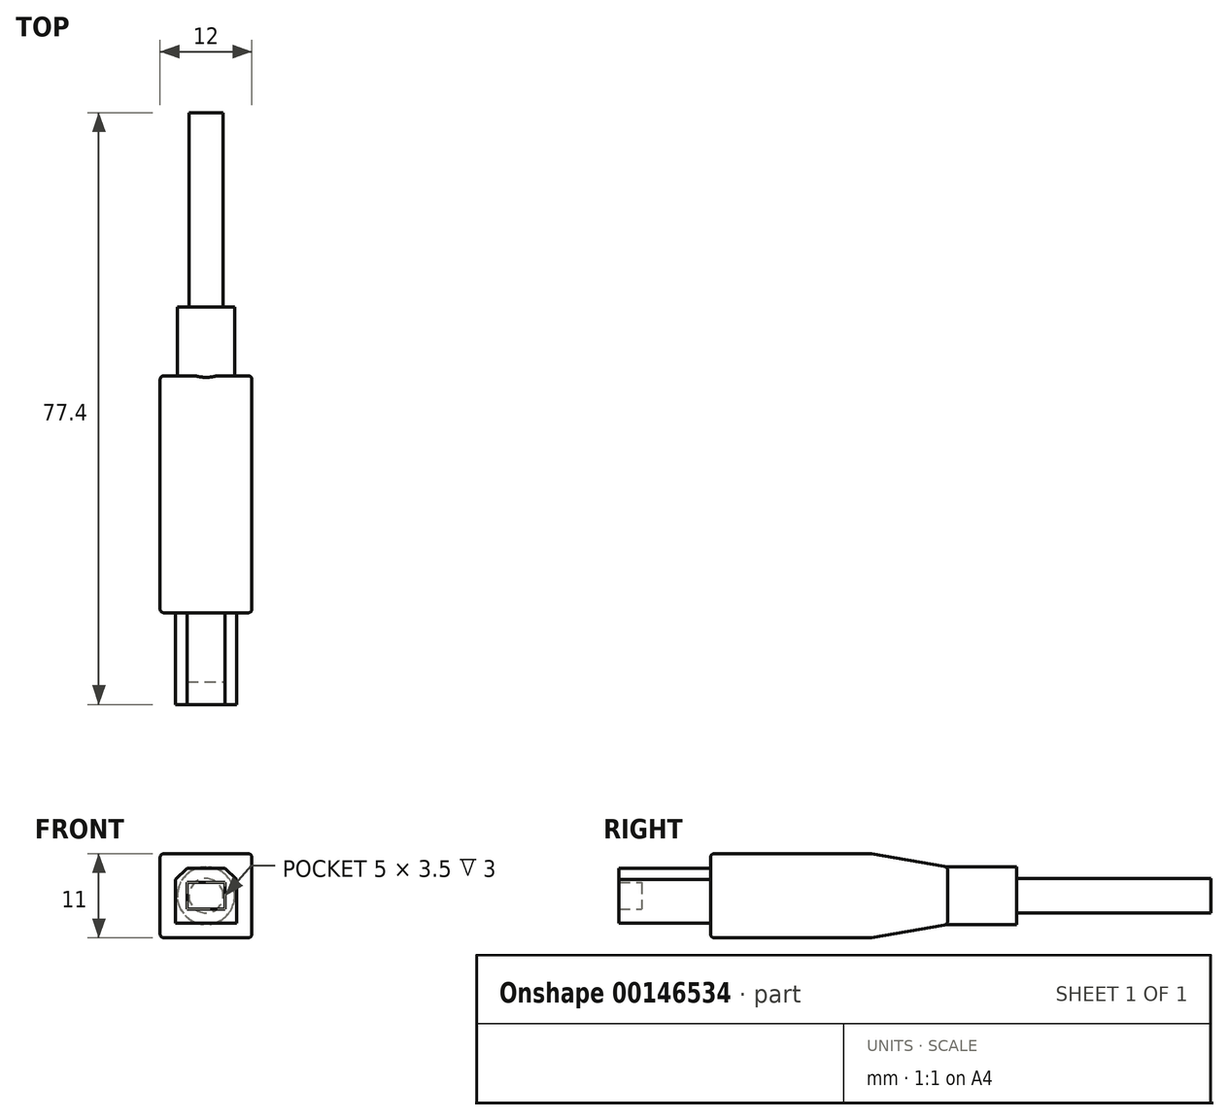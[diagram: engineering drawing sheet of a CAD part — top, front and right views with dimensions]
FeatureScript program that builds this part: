
annotation { "Feature Type Name" : "Feature", "Feature Type Description" : "" }
export const myFeature = defineFeature(function(context is Context, id is Id, definition is map)
    precondition{}
    {
        {
            var Q0;
            Q0=qCreatedBy(makeId("Front.planeOp"),FACE);
            var sketch = newSketch(context, id + "F0", { "sketchPlane" : qUnion([Q0])});
            skLineSegment(sketch, "E0.bottom", {"start": v(6, -5.5) * mm, "end": v(-6, -5.5) * mm});
            skLineSegment(sketch, "E0.top", {"start": v(6, 5.5) * mm, "end": v(-6, 5.5) * mm});
            skLineSegment(sketch, "E0.left", {"start": v(6, -5.5) * mm, "end": v(6, 5.5) * mm});
            skLineSegment(sketch, "E0.right", {"start": v(-6, -5.5) * mm, "end": v(-6, 5.5) * mm});
            skPoint(sketch, "E0.middle", {"position": v(0, 0) * mm});
            skLineSegment(sketch, "E1.bottom", {"start": v(-2.5, 1.75) * mm, "end": v(2.5, 1.75) * mm});
            skLineSegment(sketch, "E1.top", {"start": v(-2.5, -1.75) * mm, "end": v(2.5, -1.75) * mm});
            skLineSegment(sketch, "E1.left", {"start": v(-2.5, 1.75) * mm, "end": v(-2.5, -1.75) * mm});
            skLineSegment(sketch, "E1.right", {"start": v(2.5, 1.75) * mm, "end": v(2.5, -1.75) * mm});
            skLineSegment(sketch, "E2.bottom", {"start": v(-4, 3.6) * mm, "end": v(4, 3.6) * mm});
            skLineSegment(sketch, "E2.top", {"start": v(-4, -3.6) * mm, "end": v(4, -3.6) * mm});
            skLineSegment(sketch, "E2.left", {"start": v(-4, 3.6) * mm, "end": v(-4, -3.6) * mm});
            skLineSegment(sketch, "E2.right", {"start": v(4, 3.6) * mm, "end": v(4, -3.6) * mm});
            skPoint(sketch, "E3", {"position": v(0, 3.6) * mm});
            skPoint(sketch, "E4", {"position": v(-4, 0) * mm});
            skPoint(sketch, "E5", {"position": v(-2.5, 0) * mm});
            skPoint(sketch, "E6", {"position": v(0, 1.75) * mm});
            skSolve(sketch);
        }
        {
            var Q0;
            Q0=makeQuery(id+"F0.imprint","IMPRINT",FACE,{"disambiguationData":[TD([[makeQuery(id+"F0.imprint","IMPRINT",EDGE,{"derivedFrom":sQuery(id+"F0.wireOp",EDGE,"E1.bottom")}),1.0]])]});
            extrude(context, id + "F1", {"entities" : qUnion([Q0]), "depth" : 12 * mm});
        }
        {
            var Q0;
            Q0=makeQuery(id+"F0.imprint","IMPRINT",FACE,{"disambiguationData":[TD([[makeQuery(id+"F0.imprint","IMPRINT",EDGE,{"derivedFrom":sQuery(id+"F0.wireOp",EDGE,"E1.bottom")}),-1.0]])]});
            extrude(context, id + "F2", {"entities" : qUnion([Q0]), "operationType" : NewBodyOperationType.ADD, "depth" : 9 * mm});
        }
        {
            var Q0;
            Q0=makeQuery(id+"F1.opExtrude","SWEPT_EDGE",EDGE,{"disambiguationData":[OSD([sQuery(id+"F0.wireOp",EDGE,"E2.bottom"),sQuery(id+"F0.wireOp",EDGE,"E2.left")])]});
            var Q1;
            Q1=makeQuery(id+"F1.opExtrude","SWEPT_EDGE",EDGE,{"disambiguationData":[OSD([sQuery(id+"F0.wireOp",EDGE,"E2.bottom"),sQuery(id+"F0.wireOp",EDGE,"E2.right")])]});
            chamfer(context, id + "F3", {"entities" : qUnion([Q0, Q1]), "width" : 1.5 * mm, "tangentPropagation" : true});
        }
        {
            var Q0;
            Q0=makeQuery(id+"F0.imprint","IMPRINT",FACE,{"disambiguationData":[TD([[makeQuery(id+"F0.imprint","IMPRINT",EDGE,{"derivedFrom":sQuery(id+"F0.wireOp",EDGE,"E0.bottom")}),-1.0]])]});
            var Q1;
            Q1=makeQuery(id+"F0.imprint","IMPRINT",FACE,{"disambiguationData":[TD([[makeQuery(id+"F0.imprint","IMPRINT",EDGE,{"derivedFrom":sQuery(id+"F0.wireOp",EDGE,"E1.bottom")}),1.0]])]});
            var Q2;
            Q2=makeQuery(id+"F0.imprint","IMPRINT",FACE,{"disambiguationData":[TD([[makeQuery(id+"F0.imprint","IMPRINT",EDGE,{"derivedFrom":sQuery(id+"F0.wireOp",EDGE,"E1.bottom")}),-1.0]])]});
            extrude(context, id + "F4", {"entities" : qUnion([Q0, Q1, Q2]), "operationType" : NewBodyOperationType.ADD, "oppositeDirection" : true, "depth" : 31 * mm});
        }
        {
            var Q0;
            Q0=makeQuery(id+"F4.opExtrude","CAP_EDGE",EDGE,{"disambiguationData":[OSD([sQuery(id+"F0.wireOp",EDGE,"E0.top")])],"isStart":false});
            var Q1;
            Q1=makeQuery(id+"F4.opExtrude","CAP_EDGE",EDGE,{"disambiguationData":[OSD([sQuery(id+"F0.wireOp",EDGE,"E0.bottom")])],"isStart":false});
            chamfer(context, id + "F5", {"entities" : qUnion([Q0, Q1]), "chamferType" : ChamferType.TWO_OFFSETS, "width1" : 10 * mm, "oppositeDirection" : false, "width2" : 1.75 * mm, "tangentPropagation" : true});
        }
        {
            var Q0;
            Q0=makeQuery(id+"F4.opExtrude","SWEPT_FACE",FACE,{"disambiguationData":[OSD([sQuery(id+"F0.wireOp",EDGE,"E0.right")])]});
            var Q1;
            Q1=makeQuery(id+"F4.opExtrude","SWEPT_FACE",FACE,{"disambiguationData":[OSD([sQuery(id+"F0.wireOp",EDGE,"E0.left")])]});
            var Q2;
            Q2=makeQuery(id+"F4.opExtrude","SWEPT_FACE",FACE,{"disambiguationData":[OSD([sQuery(id+"F0.wireOp",EDGE,"E0.top")])]});
            var Q3;
            Q3=makeQuery(id+"F4.opExtrude","SWEPT_FACE",FACE,{"disambiguationData":[OSD([sQuery(id+"F0.wireOp",EDGE,"E0.bottom")])]});
            var Q4;
            Q4=makeQuery(id+"F4.opExtrude","CAP_FACE",FACE,{"disambiguationData":[OSD([sQuery(id+"F0.wireOp",EDGE,"E0.bottom"),sQuery(id+"F0.wireOp",EDGE,"E0.top"),sQuery(id+"F0.wireOp",EDGE,"E0.left"),sQuery(id+"F0.wireOp",EDGE,"E0.right")])],"isStart":false});
            fillet(context, id + "F6", {"entities" : qUnion([Q0, Q1, Q2, Q3, Q4]), "radius" : .5 * mm, "tangentPropagation" : true, "allowEdgeOverflow" : false});
        }
        {
            var Q0;
            Q0=makeQuery(id+"F4.opExtrude","CAP_FACE",FACE,{"disambiguationData":[OSD([sQuery(id+"F0.wireOp",EDGE,"E0.bottom"),sQuery(id+"F0.wireOp",EDGE,"E0.top"),sQuery(id+"F0.wireOp",EDGE,"E0.left"),sQuery(id+"F0.wireOp",EDGE,"E0.right")])],"isStart":false});
            var sketch = newSketch(context, id + "F7", { "sketchPlane" : qUnion([Q0])});
            skCircle(sketch, "E7", {"center": v(0, 0) * mm, "radius": 3.75 * mm});
            skSolve(sketch);
        }
        {
            var Q0;
            {var subQ0=sQuery(id+"F7.wireOp",EDGE,"E7");var subQ1=sQuery(id+"F0.wireOp",EDGE,"E0.top");var subQ2=sQuery(id+"F0.wireOp",EDGE,"E0.bottom");var subQ3=makeQuery(id+"F4.opExtrude","CAP_FACE",FACE,{"disambiguationData":[OSD([subQ2,subQ1,sQuery(id+"F0.wireOp",EDGE,"E0.left"),sQuery(id+"F0.wireOp",EDGE,"E0.right")])],"isStart":false});var subQ4=subQ3;var subQ5=makeQuery(id+"F6.opFillet","BLEND_EDGE",EDGE,{"blendedFrom":[makeQuery(id+"F5.opChamfer","BLEND_EDGE",EDGE,{"blendedFrom":[makeQuery(id+"F4.opExtrude","CAP_EDGE",EDGE,{"disambiguationData":[OSD([subQ1])],"isStart":false}),subQ3],"blendedInto":[subQ3]}),subQ4],"blendedInto":[subQ4]});var subQ6=makeQuery(id+"F7.imprint","INTERSECT",VERTEX,{"disambiguationData":[OD(0.0)],"derivedFrom":[subQ5,subQ0]});Q0=makeQuery(id+"F7.imprint","IMPRINT",FACE,{"disambiguationData":[TD([[makeQuery(id+"F7.imprint","IMPRINT",EDGE,{"disambiguationData":[TD([[subQ6,-1.0]])],"derivedFrom":subQ0}),1.0]])]});}
            var Q1;
            {var subQ0=sQuery(id+"F7.wireOp",EDGE,"E7");var subQ1=sQuery(id+"F0.wireOp",EDGE,"E0.top");var subQ2=makeQuery(id+"F4.opExtrude","CAP_FACE",FACE,{"disambiguationData":[OSD([sQuery(id+"F0.wireOp",EDGE,"E0.bottom"),subQ1,sQuery(id+"F0.wireOp",EDGE,"E0.left"),sQuery(id+"F0.wireOp",EDGE,"E0.right")])],"isStart":false});var subQ3=makeQuery(id+"F6.opFillet","BLEND_EDGE",EDGE,{"blendedFrom":[makeQuery(id+"F5.opChamfer","BLEND_EDGE",EDGE,{"blendedFrom":[makeQuery(id+"F4.opExtrude","CAP_EDGE",EDGE,{"disambiguationData":[OSD([subQ1])],"isStart":false}),subQ2],"blendedInto":[subQ2]}),subQ2],"blendedInto":[subQ2]});var subQ4=makeQuery(id+"F7.imprint","INTERSECT",VERTEX,{"disambiguationData":[OD(0.0)],"derivedFrom":[subQ3,subQ0]});Q1=makeQuery(id+"F7.imprint","IMPRINT",FACE,{"disambiguationData":[TD([[makeQuery(id+"F7.imprint","IMPRINT",EDGE,{"disambiguationData":[TD([[subQ4,1.0]])],"derivedFrom":subQ0}),1.0]])]});}
            var Q2;
            {var subQ0=sQuery(id+"F7.wireOp",EDGE,"E7");var subQ1=sQuery(id+"F0.wireOp",EDGE,"E0.bottom");var subQ2=makeQuery(id+"F4.opExtrude","CAP_FACE",FACE,{"disambiguationData":[OSD([subQ1,sQuery(id+"F0.wireOp",EDGE,"E0.top"),sQuery(id+"F0.wireOp",EDGE,"E0.left"),sQuery(id+"F0.wireOp",EDGE,"E0.right")])],"isStart":false});var subQ3=makeQuery(id+"F6.opFillet","BLEND_EDGE",EDGE,{"blendedFrom":[makeQuery(id+"F5.opChamfer","BLEND_EDGE",EDGE,{"blendedFrom":[makeQuery(id+"F4.opExtrude","CAP_EDGE",EDGE,{"disambiguationData":[OSD([subQ1])],"isStart":false}),subQ2],"blendedInto":[subQ2]}),subQ2],"blendedInto":[subQ2]});var subQ4=makeQuery(id+"F7.imprint","INTERSECT",VERTEX,{"disambiguationData":[OD(0.0)],"derivedFrom":[subQ3,subQ0]});Q2=makeQuery(id+"F7.imprint","IMPRINT",FACE,{"disambiguationData":[TD([[makeQuery(id+"F7.imprint","IMPRINT",EDGE,{"disambiguationData":[TD([[subQ4,-1.0]])],"derivedFrom":subQ0}),1.0]])]});}
            extrude(context, id + "F8", {"entities" : qUnion([Q0, Q1, Q2]), "operationType" : NewBodyOperationType.ADD, "depth" : 9 * mm, "hasSecondDirection" : true, "secondDirectionBound" : SecondDirectionBoundingType.UP_TO_NEXT, "secondDirectionOppositeDirection" : true, "secondDirectionDepth" : 25.4 * mm});
        }
        {
            var Q0;
            Q0=makeQuery(id+"F8.opExtrude","CAP_FACE",FACE,{"disambiguationData":[OSD([sQuery(id+"F7.wireOp",EDGE,"E7")])],"isStart":false});
            var sketch = newSketch(context, id + "F9", { "sketchPlane" : qUnion([Q0])});
            skCircle(sketch, "E8", {"center": v(0, 0) * mm, "radius": 2.25 * mm});
            skSolve(sketch);
        }
        {
            var Q0;
            Q0=makeQuery(id+"F9.imprint","IMPRINT",FACE,{"disambiguationData":[TD([[makeQuery(id+"F9.imprint","IMPRINT",EDGE,{"derivedFrom":sQuery(id+"F9.wireOp",EDGE,"E8")}),1.0]])]});
            extrude(context, id + "F10", {"entities" : qUnion([Q0]), "operationType" : NewBodyOperationType.ADD, "depth" : 25.4 * mm});
        }
    });
